# Revit family: Safety & Protection_Barrier_UltiGroup_Automatic Barrier Arm
name_source: partatom
category: Generic Models
revit_build: Autodesk Revit Architecture 2016 (Build: 20150220_1215(x64)
units: mm (PartAtom-declared; Revit-internal decimal feet)

## family parameters
Always vertical = Yes
Can host rebar = No
Cut with Voids When Loaded = No
OmniClass Number = 23.30.80.11
OmniClass Title = Guardrails
Part Type = Normal
Room Calculation Point = No
Round Connector Dimension = Use Diameter
Shared = No
Work Plane-Based = No

## types (5) — shared parameters
Arm brace = Arm brace
Barrier Arm length = 2300 mm  [stored 7.54593 ft]
Barrier arm support = Barrier arm support
Barrier arm with caution sign = Barrier arm with caution sign
Description = Automatic Hydraulic Barrier
Fax = 07 846 2467
Led light = Led light
Manufacturer = UltiGroup
Model = Ulti Automatic Barrier Arm - B680H
Send Message = http://ultigroup.co.nz
Stainless Steel = Stainless Steel
URL = http://ultigroup.co.nz
zero-valued in all types: InstallationGroup_ANZRS, ModifiedIssue_ANZRS

## per-type parameters (varying)
| type | Barrier post |
| Type 1 | Barrier arm post |
| Type 2 Stainless Steel | Post - Stainless Steel |
| Type 2 Blue | Post - Blue |
| Type 2 Pure White | Post - Pure White |
| Type 2 Aluminium Grey | Post - Aluminium Grey |

note: [stored X ft] marks values corroborated as IEEE doubles in the binary element streams (Revit-internal decimal feet)

## geometry (parser evidence)
native form markers: Blend x2, Sweep x3
no freeform markers — native parametric forms only
